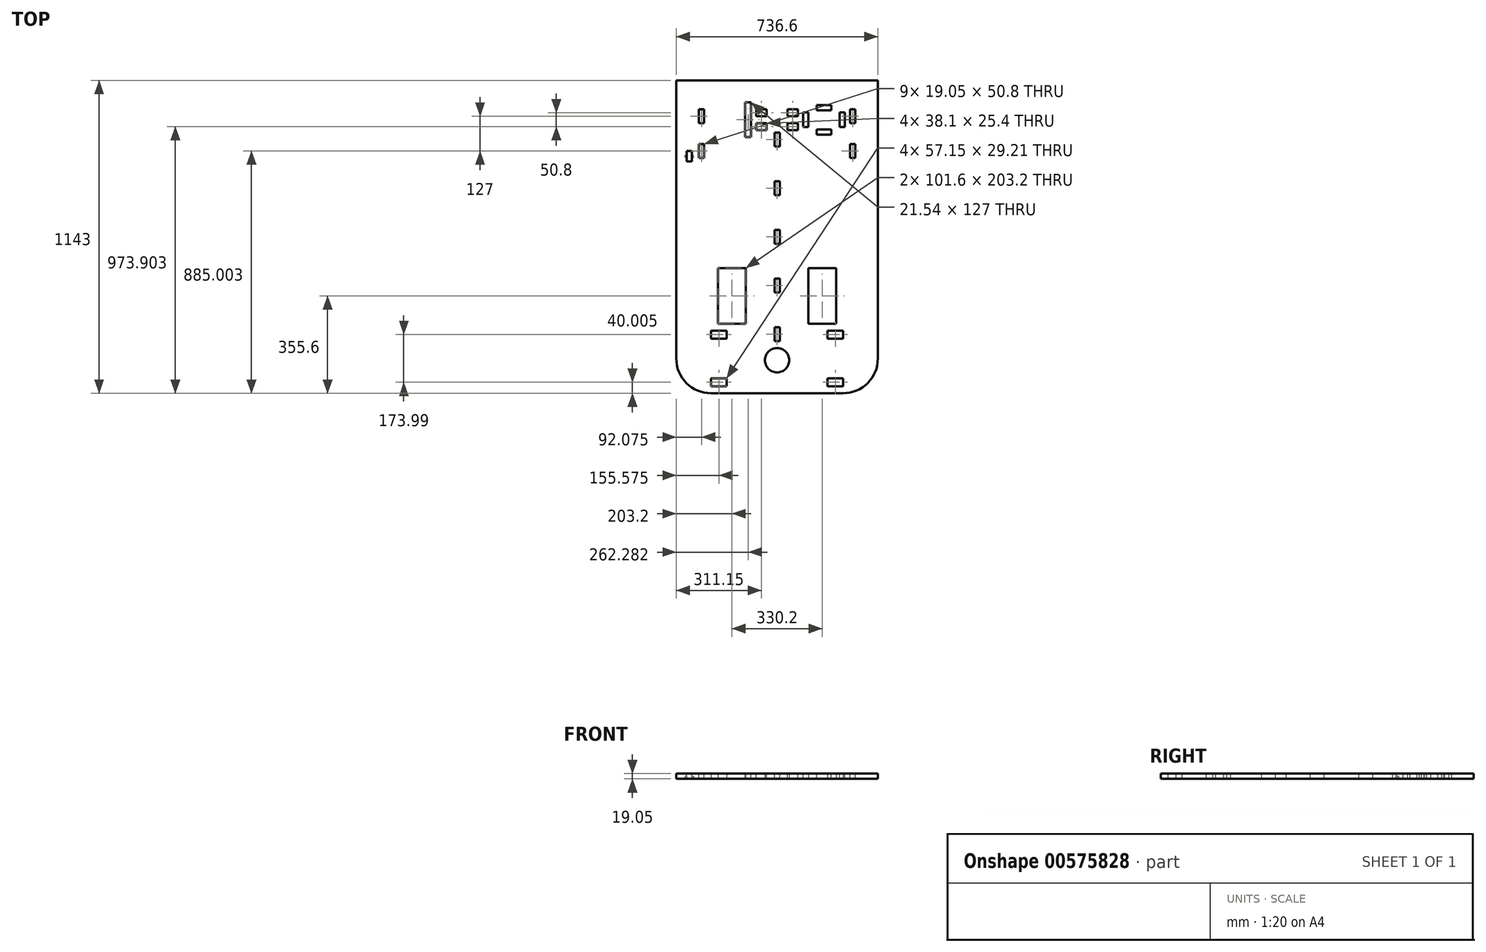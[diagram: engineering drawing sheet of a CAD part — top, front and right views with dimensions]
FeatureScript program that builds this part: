
annotation { "Feature Type Name" : "Feature", "Feature Type Description" : "" }
export const myFeature = defineFeature(function(context is Context, id is Id, definition is map)
    precondition{}
    {
        {
            var Q0;
            Q0=qCreatedBy(makeId("Top.planeOp"),FACE);
            var sketch = newSketch(context, id + "F0", { "sketchPlane" : qUnion([Q0])});
            skLineSegment(sketch, "E0.bottom", {"start": v(0, 0) * mm, "end": v(736.6, 0) * mm});
            skLineSegment(sketch, "E0.top", {"start": v(0, -1143) * mm, "end": v(736.6, -1143) * mm});
            skLineSegment(sketch, "E0.left", {"start": v(0, 0) * mm, "end": v(0, -1143) * mm});
            skLineSegment(sketch, "E0.right", {"start": v(736.6, 0) * mm, "end": v(736.6, -1143) * mm});
            skLineSegment(sketch, "E1", {"start": v(254, -889) * mm, "end": v(0, -889) * mm});
            skLineSegment(sketch, "E2", {"start": v(482.6, -889) * mm, "end": v(736.6, -889) * mm});
            skLineSegment(sketch, "E3", {"start": v(254, -889) * mm, "end": v(482.6, -889) * mm});
            skLineSegment(sketch, "E4.bottom", {"start": v(482.6, -889) * mm, "end": v(584.2, -889) * mm});
            skLineSegment(sketch, "E4.top", {"start": v(482.6, -685.8) * mm, "end": v(584.2, -685.8) * mm});
            skLineSegment(sketch, "E4.left", {"start": v(482.6, -889) * mm, "end": v(482.6, -685.8) * mm});
            skLineSegment(sketch, "E4.right", {"start": v(584.2, -889) * mm, "end": v(584.2, -685.8) * mm});
            skLineSegment(sketch, "E5.bottom", {"start": v(254, -685.8) * mm, "end": v(152.4, -685.8) * mm});
            skLineSegment(sketch, "E5.top", {"start": v(254, -889) * mm, "end": v(152.4, -889) * mm});
            skLineSegment(sketch, "E5.left", {"start": v(254, -685.8) * mm, "end": v(254, -889) * mm});
            skLineSegment(sketch, "E5.right", {"start": v(152.4, -685.8) * mm, "end": v(152.4, -889) * mm});
            skLineSegment(sketch, "E6.bottom", {"start": v(358.78, -1143) * mm, "end": v(377.83, -1143) * mm});
            skLineSegment(sketch, "E6.top", {"start": v(358.77, 0) * mm, "end": v(377.82, 0) * mm});
            skCircle(sketch, "E7", {"center": v(368.3, -1022.35) * mm, "radius": 44.45 * mm});
            skLineSegment(sketch, "E8.bottom", {"start": v(127, -914.4) * mm, "end": v(184.15, -914.4) * mm});
            skLineSegment(sketch, "E8.top", {"start": v(127, -943.6) * mm, "end": v(184.15, -943.6) * mm});
            skLineSegment(sketch, "E8.left", {"start": v(127, -914.4) * mm, "end": v(127, -943.6) * mm});
            skLineSegment(sketch, "E8.right", {"start": v(184.15, -914.4) * mm, "end": v(184.15, -943.6) * mm});
            skLineSegment(sketch, "E9.bottom", {"start": v(184.15, -1088.39) * mm, "end": v(127, -1088.39) * mm});
            skLineSegment(sketch, "E9.top", {"start": v(184.15, -1117.6) * mm, "end": v(127, -1117.6) * mm});
            skLineSegment(sketch, "E9.left", {"start": v(184.15, -1088.39) * mm, "end": v(184.15, -1117.6) * mm});
            skLineSegment(sketch, "E9.right", {"start": v(127, -1088.39) * mm, "end": v(127, -1117.6) * mm});
            skLineSegment(sketch, "E10.bottom", {"start": v(552.45, -914.4) * mm, "end": v(609.6, -914.4) * mm});
            skLineSegment(sketch, "E10.top", {"start": v(552.45, -943.6) * mm, "end": v(609.6, -943.6) * mm});
            skLineSegment(sketch, "E10.left", {"start": v(552.45, -914.4) * mm, "end": v(552.45, -943.6) * mm});
            skLineSegment(sketch, "E10.right", {"start": v(609.6, -914.4) * mm, "end": v(609.6, -943.6) * mm});
            skLineSegment(sketch, "E11.bottom", {"start": v(552.45, -1088.39) * mm, "end": v(609.6, -1088.39) * mm});
            skLineSegment(sketch, "E11.top", {"start": v(552.45, -1117.6) * mm, "end": v(609.6, -1117.6) * mm});
            skLineSegment(sketch, "E11.left", {"start": v(552.45, -1088.39) * mm, "end": v(552.45, -1117.6) * mm});
            skLineSegment(sketch, "E11.right", {"start": v(609.6, -1088.39) * mm, "end": v(609.6, -1117.6) * mm});
            skSolve(sketch);
        }
        {
            var Q0;
            {var subQ4=sQuery(id+"F0.wireOp",EDGE,"E0.bottom");var subQ6=sQuery(id+"F0.wireOp",EDGE,"E0.left");var subQ7=makeQuery(id+"F0.imprint","INTERSECT",VERTEX,{"derivedFrom":[subQ4,subQ6]});Q0=makeQuery(id+"F0.imprint","IMPRINT",FACE,{"disambiguationData":[TD([[makeQuery(id+"F0.imprint","IMPRINT",EDGE,{"disambiguationData":[TD([[subQ7,-1.0]])],"derivedFrom":subQ4}),-1.0]])]});}
            var Q1;
            {var subQ4=sQuery(id+"F0.wireOp",EDGE,"E0.right");var subQ5=sQuery(id+"F0.wireOp",EDGE,"E0.bottom");var subQ6=makeQuery(id+"F0.imprint","INTERSECT",VERTEX,{"derivedFrom":[subQ5,subQ4]});Q1=makeQuery(id+"F0.imprint","IMPRINT",FACE,{"disambiguationData":[TD([[makeQuery(id+"F0.imprint","IMPRINT",EDGE,{"disambiguationData":[TD([[subQ6,1.0]])],"derivedFrom":subQ5}),-1.0]])]});}
            var Q2;
            {var subQ5=sQuery(id+"F0.wireOp",EDGE,"6jF9B1wz-Iy1n-dTOk-jLm3-9TtPmhuf7fDK");Q2=makeQuery(id+"F0.imprint","IMPRINT",FACE,{"disambiguationData":[TD([[makeQuery(id+"F0.imprint","IMPRINT",EDGE,{"derivedFrom":subQ5}),1.0]])]});}
            var Q3;
            {var subQ1=sQuery(id+"F0.wireOp",EDGE,"E0.top");var subQ5=sQuery(id+"F0.wireOp",EDGE,"E0.right");var subQ6=makeQuery(id+"F0.imprint","INTERSECT",VERTEX,{"derivedFrom":[subQ1,subQ5]});Q3=makeQuery(id+"F0.imprint","IMPRINT",FACE,{"disambiguationData":[TD([[makeQuery(id+"F0.imprint","IMPRINT",EDGE,{"disambiguationData":[TD([[subQ6,1.0]])],"derivedFrom":subQ1}),1.0]])]});}
            var Q4;
            {var subQ5=sQuery(id+"F0.wireOp",EDGE,"E3");Q4=makeQuery(id+"F0.imprint","IMPRINT",FACE,{"disambiguationData":[TD([[makeQuery(id+"F0.imprint","IMPRINT",EDGE,{"derivedFrom":subQ5}),-1.0]])]});}
            var Q5;
            {var subQ1=sQuery(id+"F0.wireOp",EDGE,"E0.top");var subQ6=sQuery(id+"F0.wireOp",EDGE,"E0.left");var subQ8=makeQuery(id+"F0.imprint","INTERSECT",VERTEX,{"derivedFrom":[subQ1,subQ6]});Q5=makeQuery(id+"F0.imprint","IMPRINT",FACE,{"disambiguationData":[TD([[makeQuery(id+"F0.imprint","IMPRINT",EDGE,{"disambiguationData":[TD([[subQ8,-1.0]])],"derivedFrom":subQ1}),1.0]])]});}
            var Q6;
            {var subQ4=sQuery(id+"F0.wireOp",EDGE,"PgYw0lhK-NhyM-qsrp-OKeA-oSEAwgKZywL6");var subQ6=sQuery(id+"F0.wireOp",EDGE,"E0.left");var subQ7=makeQuery(id+"F0.imprint","INTERSECT",VERTEX,{"derivedFrom":[subQ6,subQ4]});Q6=makeQuery(id+"F0.imprint","IMPRINT",FACE,{"disambiguationData":[TD([[makeQuery(id+"F0.imprint","IMPRINT",EDGE,{"disambiguationData":[TD([[subQ7,-1.0]])],"derivedFrom":subQ6}),1.0]])]});}
            var Q7;
            {var subQ6=sQuery(id+"F0.wireOp",EDGE,"E0.right");var subQ8=sQuery(id+"F0.wireOp",EDGE,"mZ7gxWMp-Va0r-jFa7-mjZr-zzqUILN0IULD");var subQ10=makeQuery(id+"F0.imprint","INTERSECT",VERTEX,{"derivedFrom":[subQ6,subQ8]});Q7=makeQuery(id+"F0.imprint","IMPRINT",FACE,{"disambiguationData":[TD([[makeQuery(id+"F0.imprint","IMPRINT",EDGE,{"disambiguationData":[TD([[subQ10,-1.0]])],"derivedFrom":subQ6}),-1.0]])]});}
            var Q8;
            {var subQ0=sQuery(id+"F0.wireOp",EDGE,"9Oeek9CY-Mlmo-Y77X-eGLQ-R2eOMjpZXaY7");Q8=makeQuery(id+"F0.imprint","IMPRINT",FACE,{"disambiguationData":[TD([[makeQuery(id+"F0.imprint","IMPRINT",EDGE,{"derivedFrom":subQ0}),-1.0]])]});}
            var Q9;
            {var subQ3=sQuery(id+"F0.wireOp",EDGE,"uwOTQWjz-tfaK-oHf6-HUkZ-OVT0mFRTG2pC");Q9=makeQuery(id+"F0.imprint","IMPRINT",FACE,{"disambiguationData":[TD([[makeQuery(id+"F0.imprint","IMPRINT",EDGE,{"derivedFrom":subQ3}),1.0]])]});}
            var Q10;
            {var subQ0=sQuery(id+"F0.wireOp",EDGE,"9Oeek9CY-Mlmo-Y77X-eGLQ-R2eOMjpZXaY7");Q10=makeQuery(id+"F0.imprint","IMPRINT",FACE,{"disambiguationData":[TD([[makeQuery(id+"F0.imprint","IMPRINT",EDGE,{"derivedFrom":subQ0}),1.0]])]});}
            var Q11;
            {var subQ0=sQuery(id+"F0.wireOp",EDGE,"bur5Nzq2-AOgE-slBb-wtFB-ZEBYxaLUXZll");Q11=makeQuery(id+"F0.imprint","IMPRINT",FACE,{"disambiguationData":[TD([[makeQuery(id+"F0.imprint","IMPRINT",EDGE,{"derivedFrom":subQ0}),-1.0]])]});}
            var Q12;
            {var subQ0=sQuery(id+"F0.wireOp",EDGE,"bBYh8qPg-VJpD-ATPU-KMST-VUP1mH8g6FiZ");Q12=makeQuery(id+"F0.imprint","IMPRINT",FACE,{"disambiguationData":[TD([[makeQuery(id+"F0.imprint","IMPRINT",EDGE,{"derivedFrom":subQ0}),1.0]])]});}
            var Q13;
            {var subQ0=sQuery(id+"F0.wireOp",EDGE,"ABa26YR5-z7Pq-xD0W-UePb-3MjeifBuwXH5");Q13=makeQuery(id+"F0.imprint","IMPRINT",FACE,{"disambiguationData":[TD([[makeQuery(id+"F0.imprint","IMPRINT",EDGE,{"derivedFrom":subQ0}),1.0]])]});}
            var Q14;
            {var subQ0=sQuery(id+"F0.wireOp",EDGE,"4aQ0srCT-3h21-yaMz-TBYS-d6XFSWbZfJXN");Q14=makeQuery(id+"F0.imprint","IMPRINT",FACE,{"disambiguationData":[TD([[makeQuery(id+"F0.imprint","IMPRINT",EDGE,{"derivedFrom":subQ0}),1.0]])]});}
            var Q15;
            {var subQ3=sQuery(id+"F0.wireOp",EDGE,"4aQ0srCT-3h21-yaMz-TBYS-d6XFSWbZfJXN");Q15=makeQuery(id+"F0.imprint","IMPRINT",FACE,{"disambiguationData":[TD([[makeQuery(id+"F0.imprint","IMPRINT",EDGE,{"derivedFrom":subQ3}),-1.0]])]});}
            var Q16;
            {var subQ0=sQuery(id+"F0.wireOp",EDGE,"E6.left");var subQ1=sQuery(id+"F0.wireOp",EDGE,"6jF9B1wz-Iy1n-dTOk-jLm3-9TtPmhuf7fDK");var subQ2=makeQuery(id+"F0.imprint","INTERSECT",VERTEX,{"derivedFrom":[subQ1,subQ0]});Q16=makeQuery(id+"F0.imprint","IMPRINT",FACE,{"disambiguationData":[TD([[makeQuery(id+"F0.imprint","IMPRINT",EDGE,{"disambiguationData":[TD([[subQ2,-1.0]])],"derivedFrom":subQ1}),-1.0]])]});}
            extrude(context, id + "F1", {"entities" : qUnion([Q0, Q1, Q2, Q3, Q4, Q5, Q6, Q7, Q8, Q9, Q10, Q11, Q12, Q13, Q14, Q15, Q16]), "depth" : 19.05 * mm, "offsetDistance" : 25.4 * mm});
        }
        {
            var Q0;
            Q0=makeQuery(id+"F1.opExtrude","CAP_FACE",FACE,{"disambiguationData":[OSD([sQuery(id+"F0.wireOp",EDGE,"E0.bottom"),sQuery(id+"F0.wireOp",EDGE,"E0.top"),sQuery(id+"F0.wireOp",EDGE,"E0.left"),sQuery(id+"F0.wireOp",EDGE,"E0.right"),sQuery(id+"F0.wireOp",EDGE,"cC261SCS-ny67-agv0-aPpt-ocdv9m9CUFK9.bottom"),sQuery(id+"F0.wireOp",EDGE,"cC261SCS-ny67-agv0-aPpt-ocdv9m9CUFK9.top"),sQuery(id+"F0.wireOp",EDGE,"cC261SCS-ny67-agv0-aPpt-ocdv9m9CUFK9.left"),sQuery(id+"F0.wireOp",EDGE,"cC261SCS-ny67-agv0-aPpt-ocdv9m9CUFK9.right"),sQuery(id+"F0.wireOp",EDGE,"wFHysj1X-2kNT-gYsO-PlbI-dcAtBc6FzGMg.bottom"),sQuery(id+"F0.wireOp",EDGE,"wFHysj1X-2kNT-gYsO-PlbI-dcAtBc6FzGMg.top"),sQuery(id+"F0.wireOp",EDGE,"wFHysj1X-2kNT-gYsO-PlbI-dcAtBc6FzGMg.left"),sQuery(id+"F0.wireOp",EDGE,"wFHysj1X-2kNT-gYsO-PlbI-dcAtBc6FzGMg.right"),sQuery(id+"F0.wireOp",EDGE,"E4.bottom"),sQuery(id+"F0.wireOp",EDGE,"E4.top"),sQuery(id+"F0.wireOp",EDGE,"E4.left"),sQuery(id+"F0.wireOp",EDGE,"E4.right"),sQuery(id+"F0.wireOp",EDGE,"E5.bottom"),sQuery(id+"F0.wireOp",EDGE,"E5.top"),sQuery(id+"F0.wireOp",EDGE,"E5.left"),sQuery(id+"F0.wireOp",EDGE,"E5.right"),sQuery(id+"F0.wireOp",EDGE,"E6.bottom"),sQuery(id+"F0.wireOp",EDGE,"E6.top")])],"isStart":false});
            var sketch = newSketch(context, id + "F2", { "sketchPlane" : qUnion([Q0])});
            skLineSegment(sketch, "E12.bottom", {"start": v(358.78, -546.1) * mm, "end": v(377.83, -546.1) * mm});
            skLineSegment(sketch, "E12.top", {"start": v(358.78, -596.9) * mm, "end": v(377.83, -596.9) * mm});
            skLineSegment(sketch, "E12.left", {"start": v(358.78, -546.1) * mm, "end": v(358.78, -596.9) * mm});
            skLineSegment(sketch, "E12.right", {"start": v(377.83, -546.1) * mm, "end": v(377.83, -596.9) * mm});
            skLineSegment(sketch, "E13.bottom", {"start": v(377.83, -419.1) * mm, "end": v(358.77, -419.1) * mm});
            skLineSegment(sketch, "E13.top", {"start": v(377.82, -368.3) * mm, "end": v(358.77, -368.3) * mm});
            skLineSegment(sketch, "E13.left", {"start": v(377.83, -419.1) * mm, "end": v(377.83, -368.3) * mm});
            skLineSegment(sketch, "E13.right", {"start": v(358.77, -419.1) * mm, "end": v(358.77, -368.3) * mm});
            skLineSegment(sketch, "E14.bottom", {"start": v(377.83, -723.9) * mm, "end": v(358.77, -723.9) * mm});
            skLineSegment(sketch, "E14.top", {"start": v(377.83, -774.7) * mm, "end": v(358.78, -774.7) * mm});
            skLineSegment(sketch, "E14.left", {"start": v(377.83, -723.9) * mm, "end": v(377.83, -774.7) * mm});
            skLineSegment(sketch, "E14.right", {"start": v(358.77, -723.9) * mm, "end": v(358.78, -774.7) * mm});
            skLineSegment(sketch, "E15.bottom", {"start": v(358.78, -901.7) * mm, "end": v(377.83, -901.7) * mm});
            skLineSegment(sketch, "E15.top", {"start": v(358.78, -952.5) * mm, "end": v(377.83, -952.5) * mm});
            skLineSegment(sketch, "E15.left", {"start": v(358.78, -901.7) * mm, "end": v(358.78, -952.5) * mm});
            skLineSegment(sketch, "E15.right", {"start": v(377.83, -901.7) * mm, "end": v(377.83, -952.5) * mm});
            skLineSegment(sketch, "E16.bottom", {"start": v(377.82, -241.3) * mm, "end": v(358.77, -241.3) * mm});
            skLineSegment(sketch, "E16.top", {"start": v(377.82, -190.5) * mm, "end": v(358.77, -190.5) * mm});
            skLineSegment(sketch, "E16.left", {"start": v(377.82, -241.3) * mm, "end": v(377.82, -190.5) * mm});
            skLineSegment(sketch, "E16.right", {"start": v(358.77, -241.3) * mm, "end": v(358.77, -190.5) * mm});
            skSolve(sketch);
        }
        {
            var Q0;
            Q0=makeQuery(id+"F2.imprint","IMPRINT",FACE,{"disambiguationData":[TD([[makeQuery(id+"F2.imprint","IMPRINT",EDGE,{"derivedFrom":sQuery(id+"F2.wireOp",EDGE,"E16.bottom")}),-1.0]])]});
            var Q1;
            Q1=makeQuery(id+"F2.imprint","IMPRINT",FACE,{"disambiguationData":[TD([[makeQuery(id+"F2.imprint","IMPRINT",EDGE,{"derivedFrom":sQuery(id+"F2.wireOp",EDGE,"E13.bottom")}),-1.0]])]});
            var Q2;
            Q2=makeQuery(id+"F2.imprint","IMPRINT",FACE,{"disambiguationData":[TD([[makeQuery(id+"F2.imprint","IMPRINT",EDGE,{"derivedFrom":sQuery(id+"F2.wireOp",EDGE,"E12.bottom")}),-1.0]])]});
            var Q3;
            Q3=makeQuery(id+"F2.imprint","IMPRINT",FACE,{"disambiguationData":[TD([[makeQuery(id+"F2.imprint","IMPRINT",EDGE,{"derivedFrom":sQuery(id+"F2.wireOp",EDGE,"E14.bottom")}),1.0]])]});
            var Q4;
            Q4=makeQuery(id+"F2.imprint","IMPRINT",FACE,{"disambiguationData":[TD([[makeQuery(id+"F2.imprint","IMPRINT",EDGE,{"derivedFrom":sQuery(id+"F2.wireOp",EDGE,"E15.bottom")}),-1.0]])]});
            extrude(context, id + "F3", {"entities" : qUnion([Q0, Q1, Q2, Q3, Q4]), "operationType" : NewBodyOperationType.REMOVE, "oppositeDirection" : true, "depth" : 25.4 * mm, "offsetDistance" : 25.4 * mm});
        }
        {
            var Q0;
            Q0=makeQuery(id+"F1.opExtrude","CAP_FACE",FACE,{"disambiguationData":[OSD([sQuery(id+"F0.wireOp",EDGE,"E0.bottom"),sQuery(id+"F0.wireOp",EDGE,"E0.top"),sQuery(id+"F0.wireOp",EDGE,"E0.left"),sQuery(id+"F0.wireOp",EDGE,"E0.right"),sQuery(id+"F0.wireOp",EDGE,"cC261SCS-ny67-agv0-aPpt-ocdv9m9CUFK9.bottom"),sQuery(id+"F0.wireOp",EDGE,"cC261SCS-ny67-agv0-aPpt-ocdv9m9CUFK9.top"),sQuery(id+"F0.wireOp",EDGE,"cC261SCS-ny67-agv0-aPpt-ocdv9m9CUFK9.left"),sQuery(id+"F0.wireOp",EDGE,"cC261SCS-ny67-agv0-aPpt-ocdv9m9CUFK9.right"),sQuery(id+"F0.wireOp",EDGE,"wFHysj1X-2kNT-gYsO-PlbI-dcAtBc6FzGMg.bottom"),sQuery(id+"F0.wireOp",EDGE,"wFHysj1X-2kNT-gYsO-PlbI-dcAtBc6FzGMg.top"),sQuery(id+"F0.wireOp",EDGE,"wFHysj1X-2kNT-gYsO-PlbI-dcAtBc6FzGMg.left"),sQuery(id+"F0.wireOp",EDGE,"wFHysj1X-2kNT-gYsO-PlbI-dcAtBc6FzGMg.right"),sQuery(id+"F0.wireOp",EDGE,"E4.bottom"),sQuery(id+"F0.wireOp",EDGE,"E4.top"),sQuery(id+"F0.wireOp",EDGE,"E4.left"),sQuery(id+"F0.wireOp",EDGE,"E4.right"),sQuery(id+"F0.wireOp",EDGE,"E5.bottom"),sQuery(id+"F0.wireOp",EDGE,"E5.top"),sQuery(id+"F0.wireOp",EDGE,"E5.left"),sQuery(id+"F0.wireOp",EDGE,"E5.right"),sQuery(id+"F0.wireOp",EDGE,"E6.bottom"),sQuery(id+"F0.wireOp",EDGE,"E6.top")])],"isStart":false});
            var sketch = newSketch(context, id + "F4", { "sketchPlane" : qUnion([Q0])});
            skLineSegment(sketch, "E17.bottom", {"start": v(82.55, -105.6) * mm, "end": v(101.6, -105.6) * mm});
            skLineSegment(sketch, "E17.top", {"start": v(82.55, -156.4) * mm, "end": v(101.6, -156.4) * mm});
            skLineSegment(sketch, "E17.left", {"start": v(82.55, -105.6) * mm, "end": v(82.55, -156.4) * mm});
            skLineSegment(sketch, "E17.right", {"start": v(101.6, -105.6) * mm, "end": v(101.6, -156.4) * mm});
            skLineSegment(sketch, "E18.bottom", {"start": v(82.55, -232.6) * mm, "end": v(101.6, -232.6) * mm});
            skLineSegment(sketch, "E18.top", {"start": v(82.55, -283.4) * mm, "end": v(101.6, -283.4) * mm});
            skLineSegment(sketch, "E18.left", {"start": v(82.55, -232.6) * mm, "end": v(82.55, -283.4) * mm});
            skLineSegment(sketch, "E18.right", {"start": v(101.6, -232.6) * mm, "end": v(101.6, -283.4) * mm});
            skLineSegment(sketch, "E19.bottom", {"start": v(635, -105.6) * mm, "end": v(654.05, -105.6) * mm});
            skLineSegment(sketch, "E19.top", {"start": v(635, -156.4) * mm, "end": v(654.05, -156.4) * mm});
            skLineSegment(sketch, "E19.left", {"start": v(635, -105.6) * mm, "end": v(635, -156.4) * mm});
            skLineSegment(sketch, "E19.right", {"start": v(654.05, -105.6) * mm, "end": v(654.05, -156.4) * mm});
            skLineSegment(sketch, "E20.bottom", {"start": v(635, -232.6) * mm, "end": v(654.05, -232.6) * mm});
            skLineSegment(sketch, "E20.top", {"start": v(635, -283.4) * mm, "end": v(654.05, -283.4) * mm});
            skLineSegment(sketch, "E20.left", {"start": v(635, -232.6) * mm, "end": v(635, -283.4) * mm});
            skLineSegment(sketch, "E20.right", {"start": v(654.05, -232.6) * mm, "end": v(654.05, -283.4) * mm});
            skSolve(sketch);
        }
        {
            var Q0;
            Q0 = qSketchRegion(id + "F4", true);
            extrude(context, id + "F5", {"entities" : qUnion([Q0]), "operationType" : NewBodyOperationType.REMOVE, "oppositeDirection" : true, "depth" : 25.4 * mm, "offsetDistance" : 25.4 * mm});
        }
        {
            var Q0;
            Q0=makeQuery(id+"F1.opExtrude","CAP_FACE",FACE,{"disambiguationData":[OSD([sQuery(id+"F0.wireOp",EDGE,"E0.bottom"),sQuery(id+"F0.wireOp",EDGE,"E0.top"),sQuery(id+"F0.wireOp",EDGE,"E0.left"),sQuery(id+"F0.wireOp",EDGE,"E0.right"),sQuery(id+"F0.wireOp",EDGE,"cC261SCS-ny67-agv0-aPpt-ocdv9m9CUFK9.bottom"),sQuery(id+"F0.wireOp",EDGE,"cC261SCS-ny67-agv0-aPpt-ocdv9m9CUFK9.top"),sQuery(id+"F0.wireOp",EDGE,"cC261SCS-ny67-agv0-aPpt-ocdv9m9CUFK9.left"),sQuery(id+"F0.wireOp",EDGE,"cC261SCS-ny67-agv0-aPpt-ocdv9m9CUFK9.right"),sQuery(id+"F0.wireOp",EDGE,"wFHysj1X-2kNT-gYsO-PlbI-dcAtBc6FzGMg.bottom"),sQuery(id+"F0.wireOp",EDGE,"wFHysj1X-2kNT-gYsO-PlbI-dcAtBc6FzGMg.top"),sQuery(id+"F0.wireOp",EDGE,"wFHysj1X-2kNT-gYsO-PlbI-dcAtBc6FzGMg.left"),sQuery(id+"F0.wireOp",EDGE,"wFHysj1X-2kNT-gYsO-PlbI-dcAtBc6FzGMg.right"),sQuery(id+"F0.wireOp",EDGE,"E4.bottom"),sQuery(id+"F0.wireOp",EDGE,"E4.top"),sQuery(id+"F0.wireOp",EDGE,"E4.left"),sQuery(id+"F0.wireOp",EDGE,"E4.right"),sQuery(id+"F0.wireOp",EDGE,"E5.bottom"),sQuery(id+"F0.wireOp",EDGE,"E5.top"),sQuery(id+"F0.wireOp",EDGE,"E5.left"),sQuery(id+"F0.wireOp",EDGE,"E5.right"),sQuery(id+"F0.wireOp",EDGE,"E6.bottom"),sQuery(id+"F0.wireOp",EDGE,"E6.top")])],"isStart":false});
            var sketch = newSketch(context, id + "F6", { "sketchPlane" : qUnion([Q0])});
            skLineSegment(sketch, "E21.bottom", {"start": v(292.1, -105.6) * mm, "end": v(330.2, -105.6) * mm});
            skLineSegment(sketch, "E21.top", {"start": v(292.1, -131) * mm, "end": v(330.2, -131) * mm});
            skLineSegment(sketch, "E21.left", {"start": v(292.1, -105.6) * mm, "end": v(292.1, -131) * mm});
            skLineSegment(sketch, "E21.right", {"start": v(330.2, -105.6) * mm, "end": v(330.2, -131) * mm});
            skLineSegment(sketch, "E22.bottom", {"start": v(330.2, -156.4) * mm, "end": v(292.1, -156.4) * mm});
            skLineSegment(sketch, "E22.top", {"start": v(330.2, -181.8) * mm, "end": v(292.1, -181.8) * mm});
            skLineSegment(sketch, "E22.left", {"start": v(330.2, -156.4) * mm, "end": v(330.2, -181.8) * mm});
            skLineSegment(sketch, "E22.right", {"start": v(292.1, -156.4) * mm, "end": v(292.1, -181.8) * mm});
            skLineSegment(sketch, "E23.bottom", {"start": v(444.5, -105.6) * mm, "end": v(406.4, -105.6) * mm});
            skLineSegment(sketch, "E23.top", {"start": v(444.5, -131) * mm, "end": v(406.4, -131) * mm});
            skLineSegment(sketch, "E23.left", {"start": v(444.5, -105.6) * mm, "end": v(444.5, -131) * mm});
            skLineSegment(sketch, "E23.right", {"start": v(406.4, -105.6) * mm, "end": v(406.4, -131) * mm});
            skLineSegment(sketch, "E24.bottom", {"start": v(406.4, -156.4) * mm, "end": v(444.5, -156.4) * mm});
            skLineSegment(sketch, "E24.top", {"start": v(406.4, -181.8) * mm, "end": v(444.5, -181.8) * mm});
            skLineSegment(sketch, "E24.left", {"start": v(406.4, -156.4) * mm, "end": v(406.4, -181.8) * mm});
            skLineSegment(sketch, "E24.right", {"start": v(444.5, -156.4) * mm, "end": v(444.5, -181.8) * mm});
            skPoint(sketch, "E25.endSnap0", {"position": v(92.07, -156.4) * mm});
            skLineSegment(sketch, "E26", {"start": v(330.2, -131) * mm, "end": v(330.2, -156.4) * mm, "construction": true});
            skLineSegment(sketch, "E27", {"start": v(101.6, -283.4) * mm, "end": v(635, -283.4) * mm, "construction": true});
            skLineSegment(sketch, "E28.MirrorCS", {"start": v(512.76, -108.77) * mm, "end": v(566.74, -108.77) * mm});
            skLineSegment(sketch, "E29.MirrorCS", {"start": v(566.74, -108.77) * mm, "end": v(566.74, -70.67) * mm});
            skLineSegment(sketch, "E30.MirrorCS", {"start": v(512.76, -108.77) * mm, "end": v(512.76, -70.67) * mm});
            skLineSegment(sketch, "E31.MirrorCS", {"start": v(463.55, -89.72) * mm, "end": v(615.95, -89.72) * mm});
            skLineSegment(sketch, "E32.MirrorCS", {"start": v(615.95, -89.72) * mm, "end": v(615.95, -197.67) * mm});
            skLineSegment(sketch, "E33.MirrorCS", {"start": v(596.9, -116.7) * mm, "end": v(635, -116.7) * mm});
            skLineSegment(sketch, "E34.MirrorCS", {"start": v(596.9, -116.7) * mm, "end": v(596.9, -170.68) * mm});
            skLineSegment(sketch, "E35.MirrorCS", {"start": v(596.9, -170.68) * mm, "end": v(635, -170.68) * mm});
            skLineSegment(sketch, "E36.MirrorCS", {"start": v(635, -116.7) * mm, "end": v(635, -170.68) * mm});
            skLineSegment(sketch, "E37.MirrorCS", {"start": v(482.6, -116.7) * mm, "end": v(482.6, -170.68) * mm});
            skLineSegment(sketch, "E38.MirrorCS", {"start": v(444.5, -116.7) * mm, "end": v(482.6, -116.7) * mm});
            skLineSegment(sketch, "E39.MirrorCS", {"start": v(463.55, -197.67) * mm, "end": v(615.95, -197.67) * mm});
            skLineSegment(sketch, "E40.MirrorCS", {"start": v(512.76, -178.62) * mm, "end": v(566.74, -178.62) * mm});
            skLineSegment(sketch, "E41.MirrorCS", {"start": v(512.76, -216.72) * mm, "end": v(566.74, -216.72) * mm});
            skLineSegment(sketch, "E42.MirrorCS", {"start": v(512.76, -216.72) * mm, "end": v(512.76, -178.62) * mm});
            skLineSegment(sketch, "E43.MirrorCS", {"start": v(566.74, -216.72) * mm, "end": v(566.74, -178.62) * mm});
            skLineSegment(sketch, "E44.MirrorCS", {"start": v(444.5, -170.68) * mm, "end": v(482.6, -170.68) * mm});
            skLineSegment(sketch, "E45.MirrorCS", {"start": v(444.5, -116.7) * mm, "end": v(444.5, -170.68) * mm});
            skLineSegment(sketch, "E46.MirrorCS", {"start": v(463.55, -89.72) * mm, "end": v(463.55, -197.67) * mm});
            skLineSegment(sketch, "E47.MirrorCS", {"start": v(512.76, -70.67) * mm, "end": v(566.74, -70.67) * mm});
            skLineSegment(sketch, "E48", {"start": v(292.1, -131) * mm, "end": v(292.1, -156.4) * mm, "construction": true});
            skLineSegment(sketch, "E49", {"start": v(292.1, -143.7) * mm, "end": v(273.05, -143.7) * mm, "construction": true});
            skLineSegment(sketch, "E50", {"start": v(273.05, -143.7) * mm, "end": v(273.05, -80.2) * mm});
            skLineSegment(sketch, "E51", {"start": v(273.05, -143.7) * mm, "end": v(273.05, -207.2) * mm});
            skLineSegment(sketch, "E52", {"start": v(273.05, -80.2) * mm, "end": v(251.51, -80.2) * mm});
            skLineSegment(sketch, "E53", {"start": v(273.05, -207.2) * mm, "end": v(251.51, -207.2) * mm});
            skLineSegment(sketch, "E54", {"start": v(251.51, -80.2) * mm, "end": v(251.51, -207.2) * mm});
            skSolve(sketch);
        }
        {
            var Q0;
            Q0=makeQuery(id+"F6.imprint","IMPRINT",FACE,{"disambiguationData":[TD([[makeQuery(id+"F6.imprint","IMPRINT",EDGE,{"derivedFrom":sQuery(id+"F6.wireOp",EDGE,"E21.bottom")}),-1.0]])]});
            var Q1;
            Q1=makeQuery(id+"F6.imprint","IMPRINT",FACE,{"disambiguationData":[TD([[makeQuery(id+"F6.imprint","IMPRINT",EDGE,{"derivedFrom":sQuery(id+"F6.wireOp",EDGE,"E22.bottom")}),1.0]])]});
            var Q2;
            Q2=makeQuery(id+"F6.imprint","IMPRINT",FACE,{"disambiguationData":[TD([[makeQuery(id+"F6.imprint","IMPRINT",EDGE,{"derivedFrom":sQuery(id+"F6.wireOp",EDGE,"E24.bottom")}),-1.0]])]});
            var Q3;
            Q3=makeQuery(id+"F6.imprint","IMPRINT",FACE,{"disambiguationData":[TD([[makeQuery(id+"F6.imprint","IMPRINT",EDGE,{"derivedFrom":sQuery(id+"F6.wireOp",EDGE,"E23.bottom")}),1.0]])]});
            var Q4;
            {var subQ0=sQuery(id+"F6.wireOp",EDGE,"E28.MirrorCS");Q4=makeQuery(id+"F6.imprint","IMPRINT",FACE,{"disambiguationData":[TD([[makeQuery(id+"F6.imprint","IMPRINT",EDGE,{"derivedFrom":subQ0}),1.0]])]});}
            var Q5;
            {var subQ0=sQuery(id+"F6.wireOp",EDGE,"E37.MirrorCS");Q5=makeQuery(id+"F6.imprint","IMPRINT",FACE,{"disambiguationData":[TD([[makeQuery(id+"F6.imprint","IMPRINT",EDGE,{"derivedFrom":subQ0}),-1.0]])]});}
            var Q6;
            {var subQ5=sQuery(id+"F6.wireOp",EDGE,"E40.MirrorCS");Q6=makeQuery(id+"F6.imprint","IMPRINT",FACE,{"disambiguationData":[TD([[makeQuery(id+"F6.imprint","IMPRINT",EDGE,{"derivedFrom":subQ5}),-1.0]])]});}
            var Q7;
            {var subQ0=sQuery(id+"F6.wireOp",EDGE,"E34.MirrorCS");Q7=makeQuery(id+"F6.imprint","IMPRINT",FACE,{"disambiguationData":[TD([[makeQuery(id+"F6.imprint","IMPRINT",EDGE,{"derivedFrom":subQ0}),1.0]])]});}
            var Q8;
            Q8=makeQuery(id+"F6.imprint","IMPRINT",FACE,{"disambiguationData":[TD([[makeQuery(id+"F6.imprint","IMPRINT",EDGE,{"derivedFrom":sQuery(id+"F6.wireOp",EDGE,"E50")}),1.0]])]});
            extrude(context, id + "F7", {"entities" : qUnion([Q0, Q1, Q2, Q3, Q4, Q5, Q6, Q7, Q8]), "operationType" : NewBodyOperationType.REMOVE, "oppositeDirection" : true, "depth" : 25.4 * mm, "offsetDistance" : 25.4 * mm});
        }
        {
            var Q0;
            Q0=makeQuery(id+"F1.opExtrude","SWEPT_EDGE",EDGE,{"disambiguationData":[OSD([sQuery(id+"F0.wireOp",EDGE,"E0.top"),sQuery(id+"F0.wireOp",EDGE,"E0.left")])]});
            var Q1;
            Q1=makeQuery(id+"F1.opExtrude","SWEPT_EDGE",EDGE,{"disambiguationData":[OSD([sQuery(id+"F0.wireOp",EDGE,"E0.top"),sQuery(id+"F0.wireOp",EDGE,"E0.right")])]});
            fillet(context, id + "F8", {"entities" : qUnion([Q0, Q1]), "radius" : 127 * mm, "tangentPropagation" : true, "allowEdgeOverflow" : false});
        }
        {
            var Q0;
            Q0=makeQuery(id+"F1.opExtrude","CAP_FACE",FACE,{"disambiguationData":[OSD([sQuery(id+"F0.wireOp",EDGE,"E0.bottom"),sQuery(id+"F0.wireOp",EDGE,"E0.top"),sQuery(id+"F0.wireOp",EDGE,"E0.left"),sQuery(id+"F0.wireOp",EDGE,"E0.right"),sQuery(id+"F0.wireOp",EDGE,"cC261SCS-ny67-agv0-aPpt-ocdv9m9CUFK9.bottom"),sQuery(id+"F0.wireOp",EDGE,"cC261SCS-ny67-agv0-aPpt-ocdv9m9CUFK9.top"),sQuery(id+"F0.wireOp",EDGE,"cC261SCS-ny67-agv0-aPpt-ocdv9m9CUFK9.left"),sQuery(id+"F0.wireOp",EDGE,"cC261SCS-ny67-agv0-aPpt-ocdv9m9CUFK9.right"),sQuery(id+"F0.wireOp",EDGE,"wFHysj1X-2kNT-gYsO-PlbI-dcAtBc6FzGMg.bottom"),sQuery(id+"F0.wireOp",EDGE,"wFHysj1X-2kNT-gYsO-PlbI-dcAtBc6FzGMg.top"),sQuery(id+"F0.wireOp",EDGE,"wFHysj1X-2kNT-gYsO-PlbI-dcAtBc6FzGMg.left"),sQuery(id+"F0.wireOp",EDGE,"wFHysj1X-2kNT-gYsO-PlbI-dcAtBc6FzGMg.right"),sQuery(id+"F0.wireOp",EDGE,"E4.bottom"),sQuery(id+"F0.wireOp",EDGE,"E4.top"),sQuery(id+"F0.wireOp",EDGE,"E4.left"),sQuery(id+"F0.wireOp",EDGE,"E4.right"),sQuery(id+"F0.wireOp",EDGE,"E5.bottom"),sQuery(id+"F0.wireOp",EDGE,"E5.top"),sQuery(id+"F0.wireOp",EDGE,"E5.left"),sQuery(id+"F0.wireOp",EDGE,"E5.right"),sQuery(id+"F0.wireOp",EDGE,"E6.bottom"),sQuery(id+"F0.wireOp",EDGE,"E6.top")])],"isStart":false});
            var sketch = newSketch(context, id + "F9", { "sketchPlane" : qUnion([Q0])});
            skLineSegment(sketch, "E55.bottom", {"start": v(38.1, -258) * mm, "end": v(57.15, -258) * mm});
            skLineSegment(sketch, "E55.top", {"start": v(38.1, -296.1) * mm, "end": v(57.15, -296.1) * mm});
            skLineSegment(sketch, "E55.left", {"start": v(38.1, -258) * mm, "end": v(38.1, -296.1) * mm});
            skLineSegment(sketch, "E55.right", {"start": v(57.15, -258) * mm, "end": v(57.15, -296.1) * mm});
            skLineSegment(sketch, "E56.left", {"start": v(38.1, -273.8) * mm, "end": v(38.1, -280.4) * mm});
            skLineSegment(sketch, "E57.left", {"start": v(57.15, -273.8) * mm, "end": v(57.15, -280.4) * mm});
            skSolve(sketch);
        }
        {
            var Q0;
            Q0=makeQuery(id+"F9.imprint","IMPRINT",FACE,{"disambiguationData":[TD([[makeQuery(id+"F9.imprint","IMPRINT",EDGE,{"derivedFrom":sQuery(id+"F9.wireOp",EDGE,"E55.bottom")}),-1.0]])]});
            extrude(context, id + "F10", {"entities" : qUnion([Q0]), "operationType" : NewBodyOperationType.REMOVE, "oppositeDirection" : true, "depth" : 25.4 * mm, "offsetDistance" : 25.4 * mm});
        }
        {
            var Q0;
            Q0=makeQuery(id+"F1.opExtrude","CAP_FACE",FACE,{"disambiguationData":[OSD([sQuery(id+"F0.wireOp",EDGE,"E0.bottom"),sQuery(id+"F0.wireOp",EDGE,"E0.top"),sQuery(id+"F0.wireOp",EDGE,"E0.left"),sQuery(id+"F0.wireOp",EDGE,"E0.right"),sQuery(id+"F0.wireOp",EDGE,"cC261SCS-ny67-agv0-aPpt-ocdv9m9CUFK9.bottom"),sQuery(id+"F0.wireOp",EDGE,"cC261SCS-ny67-agv0-aPpt-ocdv9m9CUFK9.top"),sQuery(id+"F0.wireOp",EDGE,"cC261SCS-ny67-agv0-aPpt-ocdv9m9CUFK9.left"),sQuery(id+"F0.wireOp",EDGE,"cC261SCS-ny67-agv0-aPpt-ocdv9m9CUFK9.right"),sQuery(id+"F0.wireOp",EDGE,"wFHysj1X-2kNT-gYsO-PlbI-dcAtBc6FzGMg.bottom"),sQuery(id+"F0.wireOp",EDGE,"wFHysj1X-2kNT-gYsO-PlbI-dcAtBc6FzGMg.top"),sQuery(id+"F0.wireOp",EDGE,"wFHysj1X-2kNT-gYsO-PlbI-dcAtBc6FzGMg.left"),sQuery(id+"F0.wireOp",EDGE,"wFHysj1X-2kNT-gYsO-PlbI-dcAtBc6FzGMg.right"),sQuery(id+"F0.wireOp",EDGE,"E4.bottom"),sQuery(id+"F0.wireOp",EDGE,"E4.top"),sQuery(id+"F0.wireOp",EDGE,"E4.left"),sQuery(id+"F0.wireOp",EDGE,"E4.right"),sQuery(id+"F0.wireOp",EDGE,"E5.bottom"),sQuery(id+"F0.wireOp",EDGE,"E5.top"),sQuery(id+"F0.wireOp",EDGE,"E5.left"),sQuery(id+"F0.wireOp",EDGE,"E5.right"),sQuery(id+"F0.wireOp",EDGE,"E6.bottom"),sQuery(id+"F0.wireOp",EDGE,"E6.top")])],"isStart":true});
            var sketch = newSketch(context, id + "F11", { "sketchPlane" : qUnion([Q0])});
            skLineSegment(sketch, "E58.bottom", {"start": v(38.1, 280.22) * mm, "end": v(31.75, 280.22) * mm});
            skLineSegment(sketch, "E58.top", {"start": v(38.1, 273.87) * mm, "end": v(31.75, 273.87) * mm});
            skLineSegment(sketch, "E58.left", {"start": v(38.1, 280.22) * mm, "end": v(38.1, 273.87) * mm});
            skLineSegment(sketch, "E58.right", {"start": v(31.75, 280.22) * mm, "end": v(31.75, 273.87) * mm});
            skLineSegment(sketch, "E59.bottom", {"start": v(57.15, 280.22) * mm, "end": v(63.5, 280.22) * mm});
            skLineSegment(sketch, "E59.top", {"start": v(57.15, 273.87) * mm, "end": v(63.5, 273.87) * mm});
            skLineSegment(sketch, "E59.left", {"start": v(57.15, 280.22) * mm, "end": v(57.15, 273.87) * mm});
            skLineSegment(sketch, "E59.right", {"start": v(63.5, 280.22) * mm, "end": v(63.5, 273.87) * mm});
            skSolve(sketch);
        }
        {
            var Q0;
            Q0=makeQuery(id+"F11.imprint","IMPRINT",FACE,{"disambiguationData":[TD([[makeQuery(id+"F11.imprint","IMPRINT",EDGE,{"derivedFrom":sQuery(id+"F11.wireOp",EDGE,"E58.bottom")}),1.0]])]});
            var Q1;
            Q1=makeQuery(id+"F11.imprint","IMPRINT",FACE,{"disambiguationData":[TD([[makeQuery(id+"F11.imprint","IMPRINT",EDGE,{"derivedFrom":sQuery(id+"F11.wireOp",EDGE,"E59.bottom")}),-1.0]])]});
            extrude(context, id + "F12", {"entities" : qUnion([Q0, Q1]), "operationType" : NewBodyOperationType.REMOVE, "oppositeDirection" : true, "depth" : 9.52 * mm, "offsetDistance" : 25.4 * mm});
        }
    });
